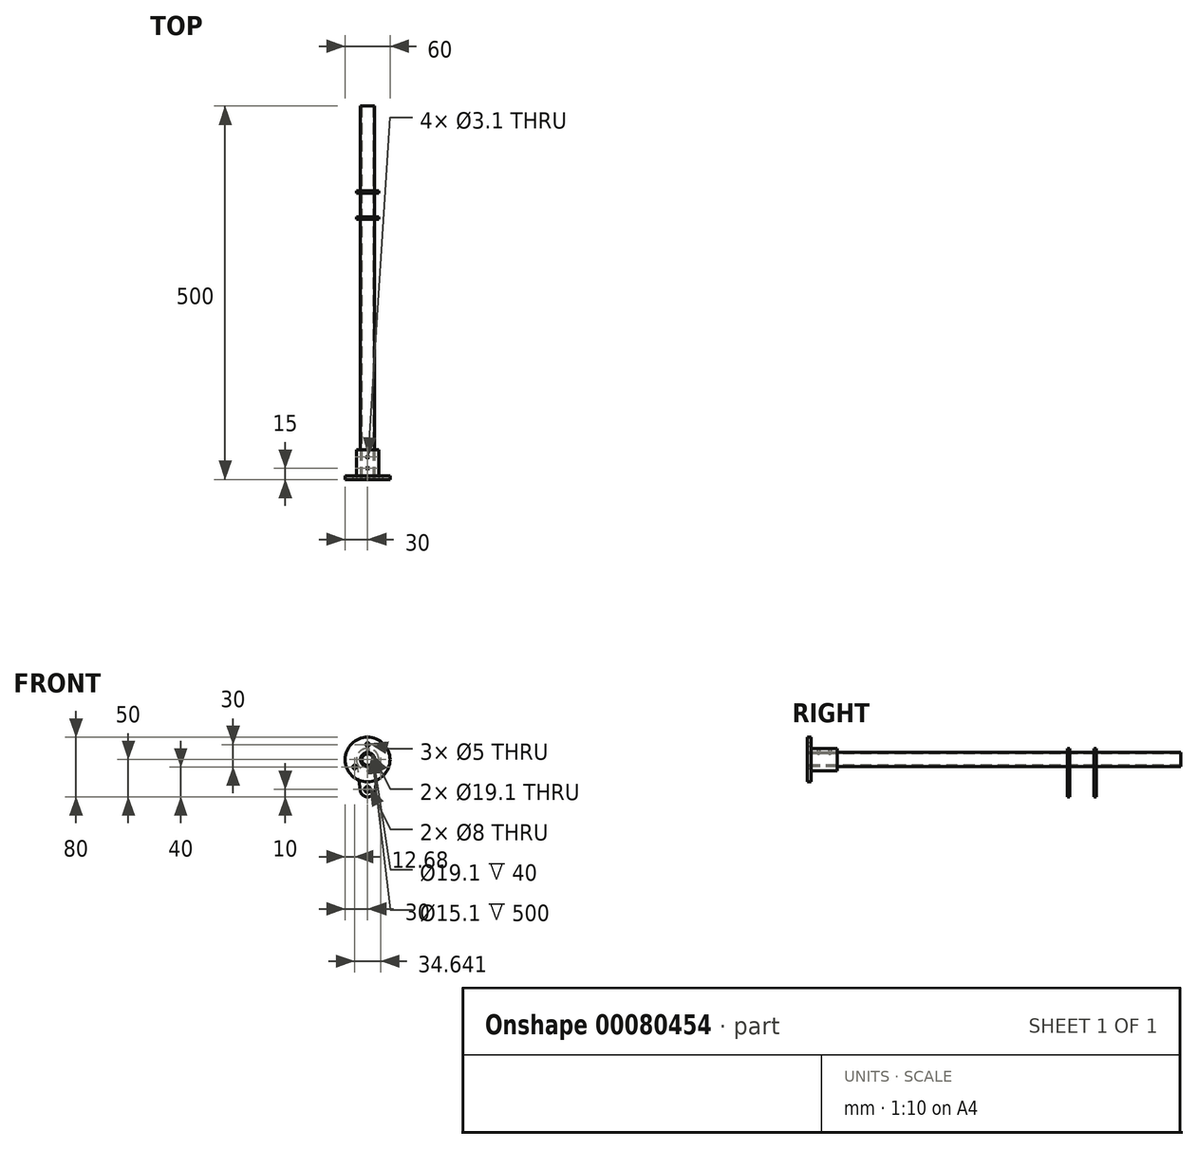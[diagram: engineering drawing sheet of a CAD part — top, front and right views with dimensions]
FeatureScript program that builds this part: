
annotation { "Feature Type Name" : "Feature", "Feature Type Description" : "" }
export const myFeature = defineFeature(function(context is Context, id is Id, definition is map)
    precondition{}
    {
        {
            var Q0;
            Q0=qCreatedBy(makeId("Front.planeOp"),FACE);
            var sketch = newSketch(context, id + "F0", { "sketchPlane" : qUnion([Q0])});
            skCircle(sketch, "E0", {"center": v(0, 0) * mm, "radius": 9.55 * mm});
            skCircle(sketch, "E1", {"center": v(0, 0) * mm, "radius": 7.55 * mm});
            skSolve(sketch);
        }
        {
            var Q0;
            Q0 = qSketchRegion(id + "F0", true);
            extrude(context, id + "F1", {"entities" : qUnion([Q0]), "oppositeDirection" : true, "depth" : 500 * mm});
        }
        {
            var Q0;
            Q0=qCreatedBy(makeId("Right.planeOp"),FACE);
            var sketch = newSketch(context, id + "F2", { "sketchPlane" : qUnion([Q0])});
            skLineSegment(sketch, "E2", {"start": v(0, -9.55) * mm, "end": v(500, -9.55) * mm, "construction": true});
            skLineSegment(sketch, "E3", {"start": v(500, 9.55) * mm, "end": v(0, 9.55) * mm, "construction": true});
            skLineSegment(sketch, "E4", {"start": v(0, 9.55) * mm, "end": v(0, -9.55) * mm, "construction": true});
            skLineSegment(sketch, "E5", {"start": v(0, 0) * mm, "end": v(72.27, 0) * mm, "construction": true});
            skLineSegment(sketch, "E6", {"start": v(0, 9.55) * mm, "end": v(0, 30) * mm});
            skLineSegment(sketch, "E7", {"start": v(0, 30) * mm, "end": v(5, 30) * mm});
            skLineSegment(sketch, "E8", {"start": v(5, 30) * mm, "end": v(5, 15) * mm});
            skLineSegment(sketch, "E9", {"start": v(5, 15) * mm, "end": v(40, 15) * mm});
            skLineSegment(sketch, "E10", {"start": v(40, 15) * mm, "end": v(40, 9.55) * mm});
            skLineSegment(sketch, "E11", {"start": v(40, 9.55) * mm, "end": v(0, 9.55) * mm});
            skSolve(sketch);
        }
        {
            var Q0;
            Q0 = qSketchRegion(id + "F2", true);
            var Q1;
            Q1=sQuery(id+"F2.wireOp",EDGE,"E5");
            revolve(context, id + "F3", {"entities" : qUnion([Q0]), "axis" : qUnion([Q1]), "revolveType" : RevolveType.FULL});
        }
        {
            var Q0;
            Q0=makeQuery(id+"F3.opRevolve","SWEPT_FACE",FACE,{"disambiguationData":[OSD([sQuery(id+"F2.wireOp",EDGE,"E6")])]});
            var sketch = newSketch(context, id + "F4", { "sketchPlane" : qUnion([Q0])});
            skCircle(sketch, "E12", {"center": v(0, 0) * mm, "radius": 20 * mm, "construction": true});
            skCircle(sketch, "E13", {"center": v(0, 20) * mm, "radius": 2.5 * mm});
            skCircle(sketch, "E14.1.0", {"center": v(-17.32, -10) * mm, "radius": 2.5 * mm});
            skCircle(sketch, "E14.2.0", {"center": v(17.32, -10) * mm, "radius": 2.5 * mm});
            skSolve(sketch);
        }
        {
            var Q0;
            Q0 = qSketchRegion(id + "F4", true);
            extrude(context, id + "F5", {"entities" : qUnion([Q0]), "operationType" : NewBodyOperationType.REMOVE, "endBound" : BoundingType.THROUGH_ALL, "oppositeDirection" : true, "depth" : 25 * mm});
        }
        {
            var Q0;
            Q0=qCreatedBy(makeId("Top.planeOp"),FACE);
            var sketch = newSketch(context, id + "F6", { "sketchPlane" : qUnion([Q0])});
            skLineSegment(sketch, "E15", {"start": v(0, 0) * mm, "end": v(0, 30) * mm, "construction": true});
            skCircle(sketch, "E16", {"center": v(0, 30) * mm, "radius": 1.55 * mm});
            skCircle(sketch, "E17", {"center": v(0, 15) * mm, "radius": 1.55 * mm});
            skSolve(sketch);
        }
        {
            var Q0;
            Q0 = qSketchRegion(id + "F6", true);
            extrude(context, id + "F7", {"entities" : qUnion([Q0]), "operationType" : NewBodyOperationType.REMOVE, "endBound" : BoundingType.THROUGH_ALL, "depth" : 25 * mm});
        }
        {
            var Q0;
            Q0=makeQuery(id+"F1.opExtrude","CAP_FACE",FACE,{"disambiguationData":[OSD([sQuery(id+"F0.wireOp",EDGE,"E0"),sQuery(id+"F0.wireOp",EDGE,"E1")])],"isStart":false});
            cPlane(context, id + "F8", {"entities" : qUnion([Q0]), "cplaneType" : CPlaneType.OFFSET, "offset" : 150 * mm, "oppositeDirection" : true, "width" : 150 * mm, "height" : 150 * mm});
        }
        {
            var Q0;
            Q0=qCreatedBy(id+"F8.planeOp",FACE);
            var sketch = newSketch(context, id + "F9", { "sketchPlane" : qUnion([Q0])});
            skCircle(sketch, "E18.0", {"center": v(0, 0) * mm, "radius": 9.55 * mm});
            skArc(sketch, "E19.0", {"start": v(14.88, -1.87) * mm, "mid": v(0, 15) * mm, "end": v(-14.88, -1.87) * mm});
            skLineSegment(sketch, "E20", {"start": v(0, 0) * mm, "end": v(0, -40) * mm, "construction": true});
            skArc(sketch, "E21", {"start": v(-9.92, -41.25) * mm, "mid": v(0, -50) * mm, "end": v(9.92, -41.25) * mm});
            skLineSegment(sketch, "E22", {"start": v(-14.88, -1.87) * mm, "end": v(-9.92, -41.25) * mm});
            skLineSegment(sketch, "E23", {"start": v(14.88, -1.87) * mm, "end": v(9.92, -41.25) * mm});
            skCircle(sketch, "E24", {"center": v(0, -40) * mm, "radius": 4 * mm});
            skSolve(sketch);
        }
        {
            var Q0;
            Q0=makeQuery(id+"F9.imprint","IMPRINT",FACE,{"disambiguationData":[TD([[makeQuery(id+"F9.imprint","IMPRINT",EDGE,{"derivedFrom":sQuery(id+"F9.wireOp",EDGE,"E18.0")}),-1.0]])]});
            extrude(context, id + "F10", {"entities" : qUnion([Q0]), "depth" : 3.2 * mm, "symmetric" : true});
        }
        {
            var Q0;
            Q0=makeQuery(id+"F10.opExtrude","SWEPT_BODY",BODY,{"disambiguationData":[OSD([sQuery(id+"F9.wireOp",EDGE,"E18.0"),sQuery(id+"F9.wireOp",EDGE,"E19.0"),sQuery(id+"F9.wireOp",EDGE,"E21"),sQuery(id+"F9.wireOp",EDGE,"E22"),sQuery(id+"F9.wireOp",EDGE,"E23"),sQuery(id+"F9.wireOp",EDGE,"E24")])]});
            transform(context, id + "F11", {"entities" : qUnion([Q0]), "transformType" : TransformType.TRANSLATION_3D, "dx" : 0 * mm, "dy" : 35 * mm, "dz" : 0 * mm, "makeCopy" : true});
        }
    });
